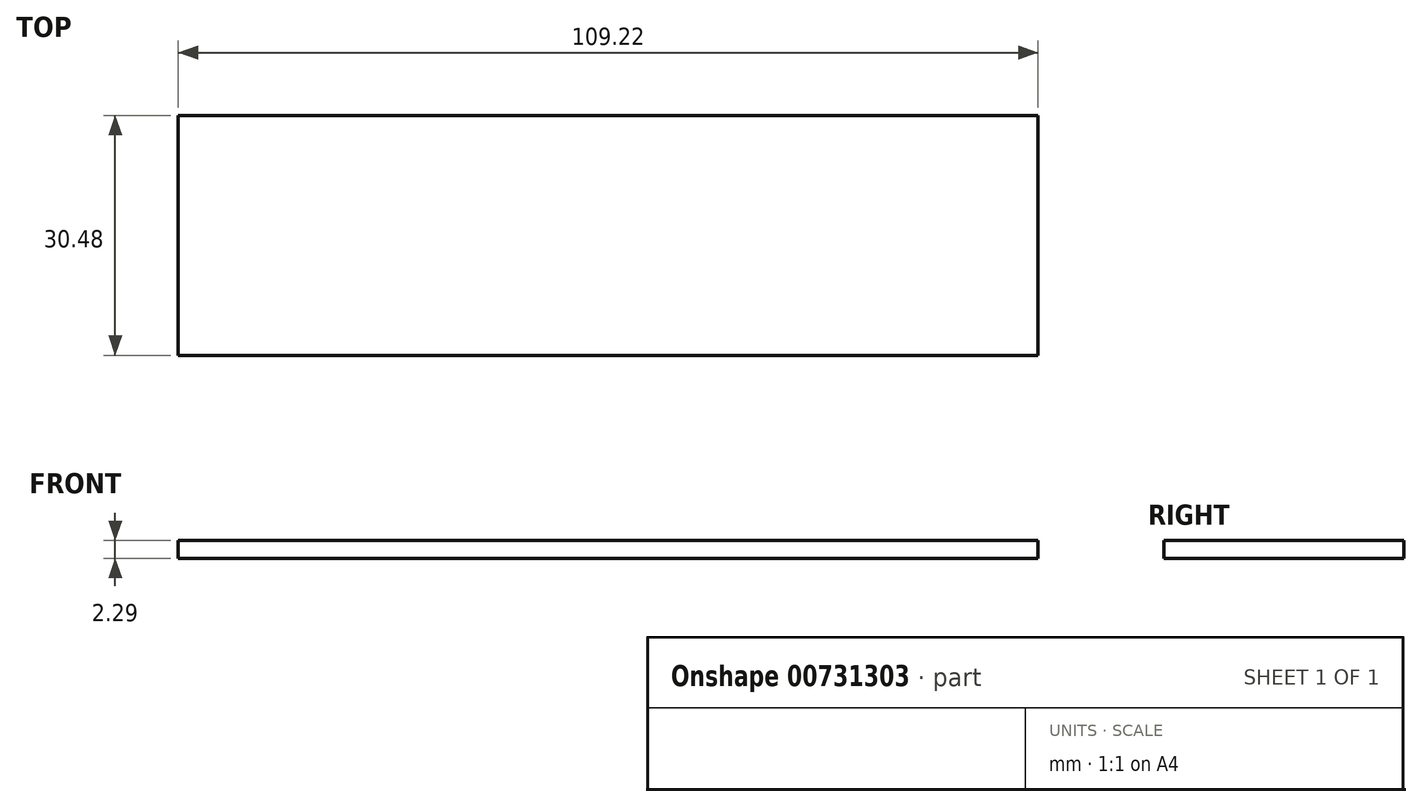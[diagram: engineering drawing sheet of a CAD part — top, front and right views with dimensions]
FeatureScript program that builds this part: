
annotation { "Feature Type Name" : "Feature", "Feature Type Description" : "" }
export const myFeature = defineFeature(function(context is Context, id is Id, definition is map)
    precondition{}
    {
        {
            var Q0;
            Q0=qCreatedBy(makeId("Top.planeOp"),FACE);
            var sketch = newSketch(context, id + "F0", { "sketchPlane" : qUnion([Q0])});
            skLineSegment(sketch, "E0.MirrorCS", {"start": v(-55.5, 13.84) * mm, "end": v(53.72, 13.84) * mm});
            skLineSegment(sketch, "E1.MirrorCS", {"start": v(-55.5, 13.84) * mm, "end": v(-55.5, 44.32) * mm});
            skLineSegment(sketch, "E2.MirrorCS", {"start": v(-55.5, 44.32) * mm, "end": v(53.72, 44.32) * mm});
            skLineSegment(sketch, "E3.MirrorCS", {"start": v(53.72, 13.84) * mm, "end": v(53.72, 44.32) * mm});
            skSolve(sketch);
        }
        {
            var Q0;
            Q0 = qSketchRegion(id + "F0", true);
            extrude(context, id + "F1", {"entities" : qUnion([Q0]), "depth" : 2.3 * mm, "offsetDistance" : 25.4 * mm});
        }
    });
